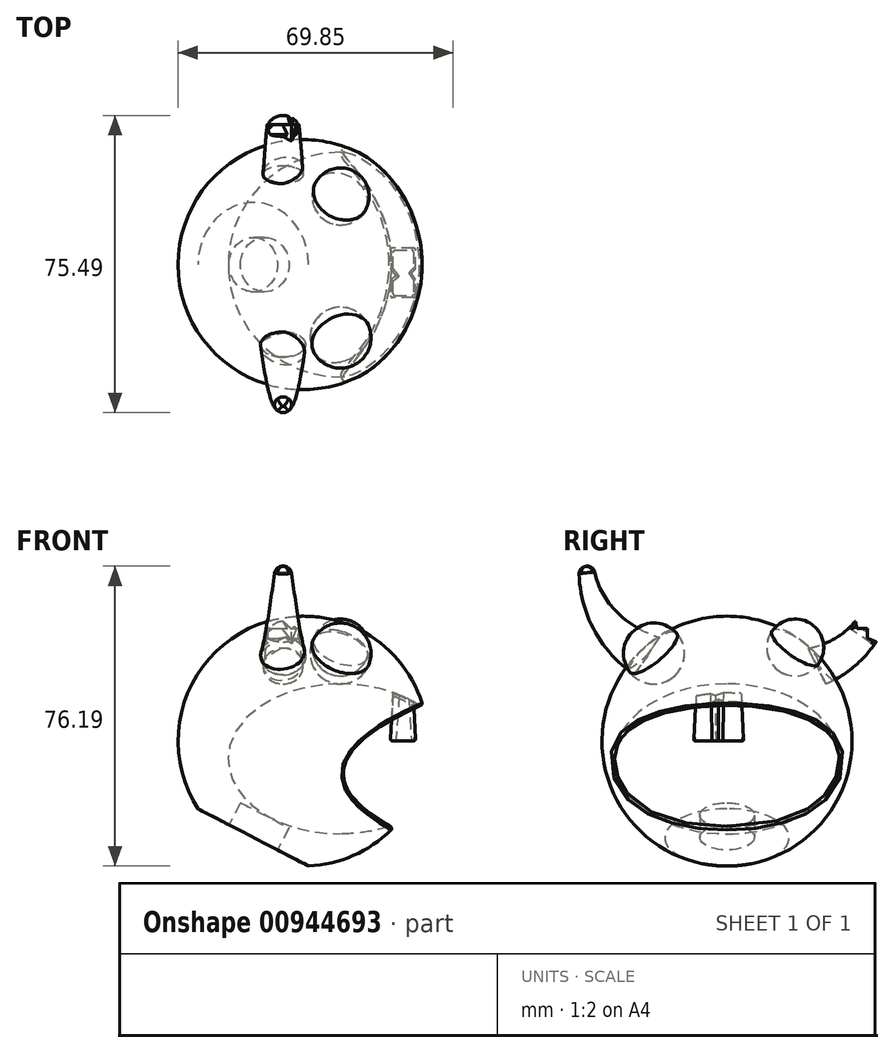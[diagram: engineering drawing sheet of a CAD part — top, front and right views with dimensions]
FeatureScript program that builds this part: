
annotation { "Feature Type Name" : "Feature", "Feature Type Description" : "" }
export const myFeature = defineFeature(function(context is Context, id is Id, definition is map)
    precondition{}
    {
        {
            var Q0;
            Q0=qCreatedBy(makeId("Front.planeOp"),FACE);
            var sketch = newSketch(context, id + "F0", { "sketchPlane" : qUnion([Q0])});
            skArc(sketch, "E0", {"start": v(0, -31.75) * mm, "mid": v(31.75, 0) * mm, "end": v(0, 31.75) * mm});
            skLineSegment(sketch, "E1", {"start": v(0, 31.75) * mm, "end": v(0, -31.75) * mm});
            skSolve(sketch);
        }
        {
            var Q0;
            Q0=qSketchRegion(id+"F0",true);
            var Q1;
            Q1=sQuery(id+"F0.wireOp",EDGE,"E1");
            revolve(context, id + "F1", {"entities" : qUnion([Q0]), "axis" : qUnion([Q1]), "revolveType" : RevolveType.FULL});
        }
        {
            var Q0;
            Q0=qCreatedBy(makeId("Right.planeOp"),FACE);
            cPlane(context, id + "F2", {"entities" : qUnion([Q0]), "cplaneType" : CPlaneType.OFFSET, "offset" : 9.52 * mm, "width" : 152.4 * mm, "height" : 152.4 * mm});
        }
        {
            var Q0;
            Q0=qCreatedBy(id+"F2.planeOp",FACE);
            var sketch = newSketch(context, id + "F3", { "sketchPlane" : qUnion([Q0])});
            skEllipse(sketch, "E2", {"center": v(0, -4.5) * mm, "majorRadius": 28.58 * mm, "minorRadius": 19.05 * mm, "majorAxis": v(1, 0)});
            skLineSegment(sketch, "E3", {"start": v(0, -23.56) * mm, "end": v(0, 14.54) * mm});
            skSolve(sketch);
        }
        {
            var Q0;
            {var subQ0=sQuery(id+"F3.wireOp",EDGE,"E3");Q0=makeQuery(id+"F3.imprint","IMPRINT",FACE,{"disambiguationData":[TD([[makeQuery(id+"F3.imprint","IMPRINT",EDGE,{"derivedFrom":subQ0}),-1.0]])]});}
            var Q1;
            Q1=sQuery(id+"F3.wireOp",EDGE,"E3");
            revolve(context, id + "F4", {"operationType" : NewBodyOperationType.REMOVE, "entities" : qUnion([Q0]), "axis" : qUnion([Q1]), "revolveType" : RevolveType.FULL});
        }
        {
            var Q0;
            Q0=qCreatedBy(makeId("Top.planeOp"),FACE);
            var sketch = newSketch(context, id + "F5", { "sketchPlane" : qUnion([Q0])});
            skLineSegment(sketch, "E4.bottom", {"start": v(22.23, -8.44) * mm, "end": v(28.58, -8.44) * mm});
            skLineSegment(sketch, "E4.top", {"start": v(22.23, 4.26) * mm, "end": v(28.58, 4.26) * mm});
            skLineSegment(sketch, "E5", {"start": v(28.58, 4.26) * mm, "end": v(28.58, -1.1) * mm});
            skLineSegment(sketch, "E6", {"start": v(28.58, -1.1) * mm, "end": v(27.56, -2.2) * mm});
            skLineSegment(sketch, "E7", {"start": v(27.56, -2.2) * mm, "end": v(28.58, -3.77) * mm});
            skLineSegment(sketch, "E8", {"start": v(28.58, -3.77) * mm, "end": v(28.58, -8.44) * mm});
            skLineSegment(sketch, "E9", {"start": v(22.23, -8.44) * mm, "end": v(22.23, -3.92) * mm});
            skLineSegment(sketch, "E10", {"start": v(22.23, -3.92) * mm, "end": v(23.57, -2.86) * mm});
            skLineSegment(sketch, "E11", {"start": v(23.57, -2.86) * mm, "end": v(22.23, -1.17) * mm});
            skLineSegment(sketch, "E12", {"start": v(22.23, -1.17) * mm, "end": v(22.23, 4.26) * mm});
            skSolve(sketch);
        }
        {
            var Q0;
            Q0=qSketchRegion(id+"F5",true);
            extrude(context, id + "F6", {"entities" : qUnion([Q0]), "endBound" : BoundingType.UP_TO_NEXT, "depth" : 25.4 * mm, "hasDraft" : true, "draftAngle" : 3 * degree, "draftPullDirection" : true});
        }
        {
            var Q0;
            Q0=makeQuery(id+"F6.opExtrude","CAP_FACE",FACE,{"disambiguationData":[OSD([sQuery(id+"F5.wireOp",EDGE,"E4.bottom"),sQuery(id+"F5.wireOp",EDGE,"E4.top"),sQuery(id+"F5.wireOp",EDGE,"E5"),sQuery(id+"F5.wireOp",EDGE,"E6"),sQuery(id+"F5.wireOp",EDGE,"E7"),sQuery(id+"F5.wireOp",EDGE,"E8"),sQuery(id+"F5.wireOp",EDGE,"E9"),sQuery(id+"F5.wireOp",EDGE,"E10"),sQuery(id+"F5.wireOp",EDGE,"E11"),sQuery(id+"F5.wireOp",EDGE,"E12")])],"isStart":true});
            var Q1;
            Q1=makeQuery(id+"F6.opExtrude","SWEPT_EDGE",EDGE,{"disambiguationData":[OSD([sQuery(id+"F5.wireOp",EDGE,"E4.top"),sQuery(id+"F5.wireOp",EDGE,"E5")])]});
            var Q2;
            Q2=makeQuery(id+"F6.opExtrude","SWEPT_EDGE",EDGE,{"disambiguationData":[OSD([sQuery(id+"F5.wireOp",EDGE,"E4.top"),sQuery(id+"F5.wireOp",EDGE,"E12")])]});
            var Q3;
            Q3=makeQuery(id+"F6.opExtrude","SWEPT_EDGE",EDGE,{"disambiguationData":[OSD([sQuery(id+"F5.wireOp",EDGE,"E4.bottom"),sQuery(id+"F5.wireOp",EDGE,"E8")])]});
            var Q4;
            Q4=makeQuery(id+"F6.opExtrude","SWEPT_EDGE",EDGE,{"disambiguationData":[OSD([sQuery(id+"F5.wireOp",EDGE,"E4.bottom"),sQuery(id+"F5.wireOp",EDGE,"E9")])]});
            fillet(context, id + "F7", {"entities" : qUnion([Q0, Q1, Q2, Q3, Q4]), "radius" : 0.5 * mm, "tangentPropagation" : true, "allowEdgeOverflow" : false});
        }
        {
            var Q0;
            Q0=makeQuery(id+"F4.boolean.opBoolean","INTERSECT",EDGE,{"derivedFrom":[makeQuery(id+"F1.opRevolve","SWEPT_FACE",FACE,{"disambiguationData":[OSD([sQuery(id+"F0.wireOp",EDGE,"E0")])]}),makeQuery(id+"F4.opRevolve","SWEPT_FACE",FACE,{"disambiguationData":[OSD([sQuery(id+"F3.wireOp",EDGE,"E2")])]})]});
            fillet(context, id + "F8", {"entities" : qUnion([Q0]), "radius" : 0.5 * mm, "tangentPropagation" : true, "allowEdgeOverflow" : false});
        }
        {
            var Q0;
            Q0=qCreatedBy(makeId("Front.planeOp"),FACE);
            var sketch = newSketch(context, id + "F9", { "sketchPlane" : qUnion([Q0])});
            skLineSegment(sketch, "E13", {"start": v(21.62, -42.16) * mm, "end": v(-43.49, -8.52) * mm});
            skLineSegment(sketch, "E14", {"start": v(-43.49, -8.52) * mm, "end": v(-43.49, -28.14) * mm});
            skLineSegment(sketch, "E15", {"start": v(-43.49, -28.14) * mm, "end": v(14.32, -57.5) * mm});
            skLineSegment(sketch, "E16", {"start": v(14.32, -57.5) * mm, "end": v(21.62, -42.16) * mm});
            skSolve(sketch);
        }
        {
            var Q0;
            Q0=qSketchRegion(id+"F9",true);
            extrude(context, id + "F10", {"entities" : qUnion([Q0]), "operationType" : NewBodyOperationType.REMOVE, "endBound" : BoundingType.SYMMETRIC, "oppositeDirection" : true, "depth" : 76.2 * mm});
        }
        {
            var Q0;
            Q0=makeQuery(id+"F10.boolean.opBoolean","COPY",FACE,{"derivedFrom":makeQuery(id+"F10.opExtrude","SWEPT_FACE",FACE,{"disambiguationData":[OSD([sQuery(id+"F9.wireOp",EDGE,"E13")])]})});
            var sketch = newSketch(context, id + "F11", { "sketchPlane" : qUnion([Q0])});
            skCircle(sketch, "E17", {"center": v(0, 0) * mm, "radius": 6.93 * mm});
            skSolve(sketch);
        }
        {
            var Q0;
            Q0=qSketchRegion(id+"F11",true);
            extrude(context, id + "F12", {"entities" : qUnion([Q0]), "operationType" : NewBodyOperationType.REMOVE, "oppositeDirection" : true, "depth" : 6.35 * mm});
        }
        {
            var Q0;
            Q0=qCreatedBy(id+"F2.planeOp",FACE);
            var sketch = newSketch(context, id + "F13", { "sketchPlane" : qUnion([Q0])});
            skCircle(sketch, "E18", {"center": v(17.34, 23.8) * mm, "radius": 7.23 * mm});
            skCircle(sketch, "E19", {"center": v(-18.57, 22.28) * mm, "radius": 7.73 * mm});
            skLineSegment(sketch, "E20", {"start": v(13.6, 17.6) * mm, "end": v(21.06, 30) * mm});
            skLineSegment(sketch, "E21", {"start": v(-13.58, 16.37) * mm, "end": v(-23.57, 28.19) * mm});
            skSolve(sketch);
        }
        {
            var Q0;
            {var subQ0=sQuery(id+"F13.wireOp",EDGE,"E21");Q0=makeQuery(id+"F13.imprint","IMPRINT",FACE,{"disambiguationData":[TD([[makeQuery(id+"F13.imprint","IMPRINT",EDGE,{"derivedFrom":subQ0}),1.0]])]});}
            var Q1;
            Q1=sQuery(id+"F13.wireOp",EDGE,"E21");
            revolve(context, id + "F14", {"entities" : qUnion([Q0]), "axis" : qUnion([Q1]), "revolveType" : RevolveType.FULL});
        }
        {
            var Q0;
            {var subQ0=sQuery(id+"F13.wireOp",EDGE,"E20");Q0=makeQuery(id+"F13.imprint","IMPRINT",FACE,{"disambiguationData":[TD([[makeQuery(id+"F13.imprint","IMPRINT",EDGE,{"derivedFrom":subQ0}),-1.0]])]});}
            var Q1;
            Q1=sQuery(id+"F13.wireOp",EDGE,"E20");
            revolve(context, id + "F15", {"entities" : qUnion([Q0]), "axis" : qUnion([Q1]), "revolveType" : RevolveType.FULL});
        }
        {
            var Q0;
            Q0=qCreatedBy(makeId("Right.planeOp"),FACE);
            cPlane(context, id + "F16", {"entities" : qUnion([Q0]), "cplaneType" : CPlaneType.OFFSET, "offset" : 5.08 * mm, "oppositeDirection" : true, "width" : 152.4 * mm, "height" : 152.4 * mm});
        }
        {
            var Q0;
            Q0=qCreatedBy(id+"F16.planeOp",FACE);
            var sketch = newSketch(context, id + "F17", { "sketchPlane" : qUnion([Q0])});
            skArc(sketch, "E22", {"start": v(-35.76, 44.45) * mm, "mid": v(-30.28, 31.5) * mm, "end": v(-20.32, 21.59) * mm});
            skArc(sketch, "E23", {"start": v(22.86, 19.05) * mm, "mid": v(33.3, 27.45) * mm, "end": v(39.44, 39.37) * mm});
            skLineSegment(sketch, "E24", {"start": v(-35.76, 44.45) * mm, "end": v(-37.97, 54.94) * mm, "construction": true});
            skLineSegment(sketch, "E25", {"start": v(-20.32, 21.59) * mm, "end": v(-9.36, 14.26) * mm, "construction": true});
            skLineSegment(sketch, "E26", {"start": v(22.86, 19.05) * mm, "end": v(14.5, 14.82) * mm, "construction": true});
            skLineSegment(sketch, "E27", {"start": v(39.44, 39.37) * mm, "end": v(42.17, 49.36) * mm, "construction": true});
            skSolve(sketch);
        }
        {
            var Q0;
            Q0=sQuery(id+"F17.wireOp",EDGE,"E26");
            var Q1;
            Q1=sQuery(id+"F17.wireOp",VERTEX,"E26.start");
            cPlane(context, id + "F18", {"entities" : qUnion([Q0, Q1]), "cplaneType" : CPlaneType.LINE_POINT, "offset" : 152.4 * mm, "width" : 152.4 * mm, "height" : 152.4 * mm});
        }
        {
            var Q0;
            Q0=qCreatedBy(id+"F18.planeOp",FACE);
            var sketch = newSketch(context, id + "F19", { "sketchPlane" : qUnion([Q0])});
            skCircle(sketch, "E28", {"center": v(-5.08, 6.67) * mm, "radius": 5.08 * mm});
            skSolve(sketch);
        }
        {
            var Q0;
            Q0=sQuery(id+"F17.wireOp",EDGE,"E25");
            var Q1;
            Q1=sQuery(id+"F17.wireOp",VERTEX,"E25.start");
            cPlane(context, id + "F20", {"entities" : qUnion([Q0, Q1]), "cplaneType" : CPlaneType.LINE_POINT, "offset" : 152.4 * mm, "width" : 152.4 * mm, "height" : 152.4 * mm});
        }
        {
            var Q0;
            Q0=qCreatedBy(id+"F20.planeOp",FACE);
            var sketch = newSketch(context, id + "F21", { "sketchPlane" : qUnion([Q0])});
            skCircle(sketch, "E29", {"center": v(5.08, 6.65) * mm, "radius": 5.72 * mm});
            skSolve(sketch);
        }
        {
            var Q0;
            Q0=sQuery(id+"F17.wireOp",VERTEX,"E24.start");
            var Q1;
            Q1=sQuery(id+"F17.wireOp",EDGE,"E24");
            cPlane(context, id + "F22", {"entities" : qUnion([Q0, Q1]), "cplaneType" : CPlaneType.LINE_POINT, "offset" : 152.4 * mm, "width" : 152.4 * mm, "height" : 152.4 * mm});
        }
        {
            var Q0;
            Q0=qCreatedBy(id+"F22.planeOp",FACE);
            var sketch = newSketch(context, id + "F23", { "sketchPlane" : qUnion([Q0])});
            skCircle(sketch, "E30", {"center": v(-5.08, -25.86) * mm, "radius": 1.9 * mm});
            skSolve(sketch);
        }
        {
            var Q0;
            Q0=sQuery(id+"F17.wireOp",EDGE,"E27");
            var Q1;
            Q1=sQuery(id+"F17.wireOp",VERTEX,"E27.start");
            cPlane(context, id + "F24", {"entities" : qUnion([Q0, Q1]), "cplaneType" : CPlaneType.LINE_POINT, "offset" : 152.4 * mm, "width" : 152.4 * mm, "height" : 152.4 * mm});
        }
        {
            var Q0;
            Q0=qCreatedBy(id+"F24.planeOp",FACE);
            var sketch = newSketch(context, id + "F25", { "sketchPlane" : qUnion([Q0])});
            skCircle(sketch, "E31", {"center": v(-5.08, 27.67) * mm, "radius": 3.18 * mm});
            skSolve(sketch);
        }
        {
            var Q0;
            Q0=qCreatedBy(id+"F16.planeOp",FACE);
            var sketch = newSketch(context, id + "F26", { "sketchPlane" : qUnion([Q0])});
            skArc(sketch, "E32", {"start": v(-37.63, 44.06) * mm, "mid": v(-33.98, 28.67) * mm, "end": v(-23.5, 16.84) * mm});
            skArc(sketch, "E33", {"start": v(25.15, 14.52) * mm, "mid": v(37.12, 24.15) * mm, "end": v(42.5, 38.53) * mm});
            skSolve(sketch);
        }
        {
            var Q1;
            Q1=qSketchRegion(id+"F21",true);
            var Q2;
            Q2=qSketchRegion(id+"F23",true);
            var Q3;
            Q3=sQuery(id+"F26.wireOp",EDGE,"E32");
            loft(context, id + "F27", {"addGuides" : true, "sheetProfilesArray" : [{ "sheetProfileEntities" : qUnion([Q1]) }, { "sheetProfileEntities" : qUnion([Q2]) }], "guidesArray" : [{ "guideEntities" : qUnion([Q3]), "guideDerivativeType" : LoftGuideDerivativeType.DEFAULT, "guideDerivativeMagnitude" : 1 }]});
        }
        {
            var Q1;
            Q1=qSketchRegion(id+"F25",true);
            var Q2;
            Q2=qSketchRegion(id+"F19",true);
            var Q3;
            Q3=sQuery(id+"F26.wireOp",EDGE,"E33");
            loft(context, id + "F28", {"addGuides" : true, "sheetProfilesArray" : [{ "sheetProfileEntities" : qUnion([Q1]) }, { "sheetProfileEntities" : qUnion([Q2]) }], "guidesArray" : [{ "guideEntities" : qUnion([Q3]), "guideDerivativeType" : LoftGuideDerivativeType.DEFAULT, "guideDerivativeMagnitude" : 1 }]});
        }
        {
            var Q0;
            Q0=makeQuery(id+"F27.opLoft","MID_CAP_EDGE",EDGE,{"disambiguationData":[OSD([sQuery(id+"F23.wireOp",EDGE,"E30"),sQuery(id+"F26.wireOp",EDGE,"E32")])],"capPos":1.0});
            fillet(context, id + "F29", {"entities" : qUnion([Q0]), "radius" : 1.9 * mm, "tangentPropagation" : true, "allowEdgeOverflow" : false});
        }
        {
            var Q0;
            Q0=qCreatedBy(id+"F16.planeOp",FACE);
            var sketch = newSketch(context, id + "F30", { "sketchPlane" : qUnion([Q0])});
            skLineSegment(sketch, "E34", {"start": v(42.34, 23.48) * mm, "end": v(35.63, 26.15) * mm});
            skLineSegment(sketch, "E35", {"start": v(35.63, 26.15) * mm, "end": v(35.63, 28.6) * mm});
            skLineSegment(sketch, "E36", {"start": v(35.63, 28.6) * mm, "end": v(33.01, 28.6) * mm});
            skLineSegment(sketch, "E37", {"start": v(33.01, 28.6) * mm, "end": v(32.03, 32.6) * mm});
            skLineSegment(sketch, "E38", {"start": v(32.03, 32.6) * mm, "end": v(36.21, 44.61) * mm});
            skLineSegment(sketch, "E39", {"start": v(36.21, 44.61) * mm, "end": v(47.25, 42.03) * mm});
            skLineSegment(sketch, "E40", {"start": v(47.25, 42.03) * mm, "end": v(42.34, 23.48) * mm});
            skSolve(sketch);
        }
        {
            var Q0;
            Q0=qSketchRegion(id+"F30",true);
            extrude(context, id + "F31", {"entities" : qUnion([Q0]), "operationType" : NewBodyOperationType.REMOVE, "endBound" : BoundingType.SYMMETRIC, "oppositeDirection" : true, "depth" : 25.4 * mm});
        }
        {
            var Q0;
            Q0=qCreatedBy(id+"F20.planeOp",FACE);
            var sketch = newSketch(context, id + "F32", { "sketchPlane" : qUnion([Q0])});
            skLineSegment(sketch, "E41", {"start": v(14.61, 39.44) * mm, "end": v(6.08, 44.55) * mm});
            skLineSegment(sketch, "E42", {"start": v(6.08, 44.55) * mm, "end": v(2.9, 41.06) * mm});
            skLineSegment(sketch, "E43", {"start": v(2.9, 41.06) * mm, "end": v(0, 47.2) * mm});
            skLineSegment(sketch, "E44", {"start": v(0, 47.2) * mm, "end": v(11, 52.42) * mm});
            skLineSegment(sketch, "E45", {"start": v(11, 52.42) * mm, "end": v(14.61, 39.44) * mm});
            skSolve(sketch);
        }
        {
            var Q0;
            Q0=qSketchRegion(id+"F32",true);
            extrude(context, id + "F33", {"entities" : qUnion([Q0]), "operationType" : NewBodyOperationType.REMOVE, "depth" : 101.6 * mm});
        }
        {
            var Q0;
            Q0=makeQuery(id+"F14.opRevolve","SWEPT_BODY",BODY,{"disambiguationData":[OSD([sQuery(id+"F13.wireOp",EDGE,"E19"),sQuery(id+"F13.wireOp",EDGE,"E21")])]});
            var Q1;
            Q1=makeQuery(id+"F15.opRevolve","SWEPT_BODY",BODY,{"disambiguationData":[OSD([sQuery(id+"F13.wireOp",EDGE,"E18"),sQuery(id+"F13.wireOp",EDGE,"E20")])]});
            var Q2;
            Q2=makeQuery(id+"F27.opLoft","SWEPT_BODY",BODY,{"disambiguationData":[OSD([makeQuery(id+"F21.imprint","IMPRINT",FACE,{"disambiguationData":[TD([[makeQuery(id+"F21.imprint","IMPRINT",EDGE,{"derivedFrom":sQuery(id+"F21.wireOp",EDGE,"E29")}),1.0]])]}),makeQuery(id+"F23.imprint","IMPRINT",FACE,{"disambiguationData":[TD([[makeQuery(id+"F23.imprint","IMPRINT",EDGE,{"derivedFrom":sQuery(id+"F23.wireOp",EDGE,"E30")}),1.0]])]}),sQuery(id+"F26.wireOp",EDGE,"E32")])]});
            var Q3;
            Q3=makeQuery(id+"F28.opLoft","SWEPT_BODY",BODY,{"disambiguationData":[OSD([makeQuery(id+"F19.imprint","IMPRINT",FACE,{"disambiguationData":[TD([[makeQuery(id+"F19.imprint","IMPRINT",EDGE,{"derivedFrom":sQuery(id+"F19.wireOp",EDGE,"E28")}),1.0]])]}),makeQuery(id+"F25.imprint","IMPRINT",FACE,{"disambiguationData":[TD([[makeQuery(id+"F25.imprint","IMPRINT",EDGE,{"derivedFrom":sQuery(id+"F25.wireOp",EDGE,"E31")}),1.0]])]}),sQuery(id+"F26.wireOp",EDGE,"E33")])]});
            var Q4;
            Q4=makeQuery(id+"F1.opRevolve","SWEPT_BODY",BODY,{"disambiguationData":[OSD([sQuery(id+"F0.wireOp",EDGE,"E0"),sQuery(id+"F0.wireOp",EDGE,"E1")])]});
            var Q5;
            Q5=makeQuery(id+"F14.opRevolve","SWEPT_FACE",FACE,{"disambiguationData":[OSD([sQuery(id+"F13.wireOp",EDGE,"E19")])]});
            var Q6;
            Q6=makeQuery(id+"F15.opRevolve","SWEPT_FACE",FACE,{"disambiguationData":[OSD([sQuery(id+"F13.wireOp",EDGE,"E18")])]});
            var Q7;
            Q7=makeQuery(id+"F28.opLoft","SWEPT_FACE",FACE,{"disambiguationData":[OSD([sQuery(id+"F19.wireOp",EDGE,"E28"),sQuery(id+"F25.wireOp",EDGE,"E31"),sQuery(id+"F26.wireOp",EDGE,"E33")])]});
            var Q8;
            Q8=makeQuery(id+"F27.opLoft","SWEPT_FACE",FACE,{"disambiguationData":[OSD([sQuery(id+"F21.wireOp",EDGE,"E29"),sQuery(id+"F23.wireOp",EDGE,"E30"),sQuery(id+"F26.wireOp",EDGE,"E32")])]});
            booleanBodies(context, id + "F34", {"operationType" : BooleanOperationType.SUBTRACTION, "tools" : qUnion([Q0, Q1, Q2, Q3]), "targets" : qUnion([Q4]), "offset" : true, "entitiesToOffset" : qUnion([Q5, Q6, Q7, Q8]), "offsetDistance" : 0.03 * mm, "keepTools" : true});
        }
    });
